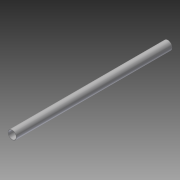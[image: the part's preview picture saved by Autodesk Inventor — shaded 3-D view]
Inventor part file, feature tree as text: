
AUTODESK INVENTOR PART (.ipt)
format: ipt  version: 2013 (Build 170138000, 138)  size: 69,632 bytes
history: native  units: in
note: dims shown in document units (in); Inventor stores cm internally (conversion verified against a paired STEP export)
features: extrude x1, sketch x1
ambient origin geometry x8: Origin, YZ Plane, XZ Plane, XY Plane, X Axis, Y Axis, Z Axis, Center Point
bodies: Solid1 (feature_tree)
feature tree (2):
  extrude  "Extrusion1"  Depth=1.33in
  sketch  "Sketch1"  dims[d0=1.5in d2=1.33in d3=26.63in d4=0.0in]
